# Revit family: DSF
name_source: partatom
category: Specialty Equipment
units: mm (PartAtom-declared; Revit-internal decimal feet)

## family parameters
Cut with Voids When Loaded = No
Host = Face
Part Type = Normal
Room Calculation Point = No
Round Connector Dimension = Use Diameter
Shared = No

## types (15) — shared parameters
ABAA Compliance = Yes
Assembly Code = C3020200
Default Elevation = 0"
Description = NSF-61 compliant expansion joint system for food production and preparation environments
Durometer Hardness of Silicone Coating (ASTM D2240) = Shore A: 35
Manufacturer = EMSEAL Joint Systems Ltd
Model = DSF
Movement (of Nominal Material Size) = +25% / -25%
Pick Resistance = No
Product Data URL = https://bit.ly
Product Documentation URL = https://bit.ly
Product Page URL = https://bit.ly
https://bit.ly
https://bit.ly
https://bit.ly
R Value Range (ASTM C518) = 2.1 per 1-inch (25mm) depth
Rate of Air Leakage (ASTM E283) = Passed
Seal Material Note = DSF is coated on the top/outer facing side with Dow DOWSIL™ 748 silicone
Staining (ASTM C510) = None
Temperature Range (ASTM C711) = 185°F (85°C) to -40°F (-40°C)
Tensile Strength (ASTM D3574) = 18 psi min; 145 kPa
Type Image = EMSEAL DSF.jpg
URL = http://www.emseal.com

## per-type parameters (varying)
| type | Depth | Quad Deep Bellow | Quad Shallow Bellow | Single Deep Bellow | Single Shallow Bellow | Triple Bellow | Triple Deep Bellow | Triple Shallow Bellow | Width |
| DSF - .5 inches | 1 3/4" | No | No | No | Yes | No | No | No | 1/2" |
| DSF - .75 inches | 1 3/4" | No | No | No | Yes | No | No | No | 3/4" |
| DSF - 1 inches | 2" | No | No | Yes | No | No | No | No | 1" |
| DSF - 1.25 inches | 2" | No | No | Yes | No | No | No | No | 1 1/4" |
| DSF - 1.5 inches | 2 1/2" | No | No | No | No | No | No | Yes | 1 1/2" |
| DSF - 1.75 inches | 2 1/2" | No | No | No | No | No | No | Yes | 1 3/4" |
| DSF - 2 inches | 2 1/2" | No | No | No | No | No | No | Yes | 2" |
| DSF - 2.25 inches | 2 1/2" | No | No | No | No | No | No | Yes | 2 1/4" |
| DSF - 2.5inches | 2 3/4" | No | No | No | No | Yes | No | No | 2 1/2" |
| DSF - 2.75 inches | 3 1/4" | No | No | No | No | No | Yes | No | 2 3/4" |
| DSF - 3 inches | 3 1/4" | No | No | No | No | No | Yes | No | 3" |
| DSF - 3.25 inches | 3 1/2" | No | Yes | No | No | No | No | No | 3 1/4" |
| DSF - 3.5 inches | 3 1/2" | No | Yes | No | No | No | No | No | 3 1/2" |
| DSF - 3.75 inches | 4" | Yes | No | No | No | No | No | No | 3 3/4" |
| DSF - 4 inches | 4" | Yes | No | No | No | No | No | No | 4" |

## geometry (parser evidence)
native form markers: Sweep x2
no freeform markers — native parametric forms only
